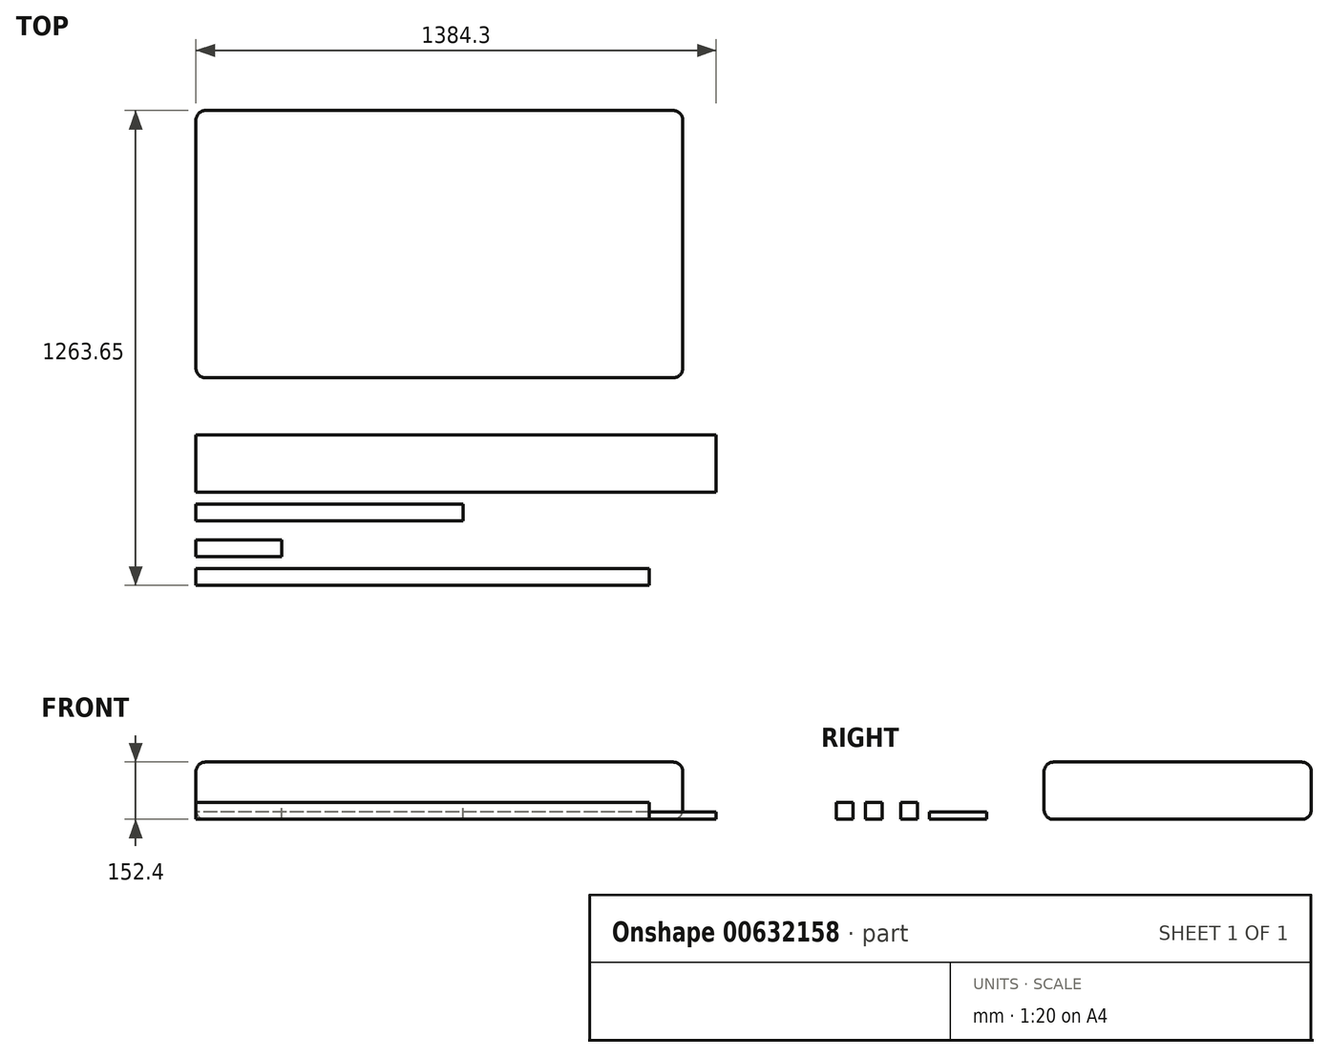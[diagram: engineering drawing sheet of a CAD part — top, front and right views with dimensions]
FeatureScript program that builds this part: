
annotation { "Feature Type Name" : "Feature", "Feature Type Description" : "" }
export const myFeature = defineFeature(function(context is Context, id is Id, definition is map)
    precondition{}
    {
        {
            var Q0;
            Q0=qCreatedBy(makeId("Right.planeOp"),FACE);
            var sketch = newSketch(context, id + "F0", { "sketchPlane" : qUnion([Q0])});
            skLineSegment(sketch, "E0.bottom", {"start": v(0, 0) * mm, "end": v(44.45, 0) * mm});
            skLineSegment(sketch, "E0.top", {"start": v(0, 44.45) * mm, "end": v(44.45, 44.45) * mm});
            skLineSegment(sketch, "E0.left", {"start": v(0, 0) * mm, "end": v(0, 44.45) * mm});
            skLineSegment(sketch, "E0.right", {"start": v(44.45, 0) * mm, "end": v(44.45, 44.45) * mm});
            skSolve(sketch);
        }
        {
            var Q0;
            Q0 = qSketchRegion(id + "F0", true);
            extrude(context, id + "F1", {"entities" : qUnion([Q0]), "depth" : 711.2 * mm, "offsetDistance" : 25.4 * mm});
        }
        {
            var Q0;
            Q0=makeQuery(id+"F1.opExtrude","SWEPT_BODY",BODY,{"disambiguationData":[OSD([sQuery(id+"F0.wireOp",EDGE,"E0.bottom"),sQuery(id+"F0.wireOp",EDGE,"E0.top"),sQuery(id+"F0.wireOp",EDGE,"E0.left"),sQuery(id+"F0.wireOp",EDGE,"E0.right")])]});
            transform(context, id + "F2", {"entities" : qUnion([Q0]), "transformType" : TransformType.TRANSLATION_3D, "dx" : 0 * mm, "dy" : 0 * mm, "dz" : 0 * mm, "makeCopy" : true});
        }
        {
            var Q0;
            Q0=qCreatedBy(makeId("Right.planeOp"),FACE);
            var sketch = newSketch(context, id + "F3", { "sketchPlane" : qUnion([Q0])});
            skLineSegment(sketch, "E1.bottom", {"start": v(-49.8, 0) * mm, "end": v(-94.25, 0) * mm});
            skLineSegment(sketch, "E1.top", {"start": v(-49.8, 44.45) * mm, "end": v(-94.25, 44.45) * mm});
            skLineSegment(sketch, "E1.left", {"start": v(-49.8, 0) * mm, "end": v(-49.8, 44.45) * mm});
            skLineSegment(sketch, "E1.right", {"start": v(-94.25, 0) * mm, "end": v(-94.25, 44.45) * mm});
            skSolve(sketch);
        }
        {
            var Q0;
            Q0 = qSketchRegion(id + "F3", true);
            extrude(context, id + "F4", {"entities" : qUnion([Q0]), "depth" : 228.6 * mm, "offsetDistance" : 25.4 * mm});
        }
        {
            var Q0;
            Q0=makeQuery(id+"F2.opPattern","COPY",BODY,{"derivedFrom":makeQuery(id+"F1.opExtrude","SWEPT_BODY",BODY,{"disambiguationData":[OSD([sQuery(id+"F0.wireOp",EDGE,"E0.bottom"),sQuery(id+"F0.wireOp",EDGE,"E0.top"),sQuery(id+"F0.wireOp",EDGE,"E0.left"),sQuery(id+"F0.wireOp",EDGE,"E0.right")])]}),"instanceName":"1"});
            deleteBodies(context, id + "F5", {"entities" : qUnion([Q0])});
        }
        {
            var Q0;
            Q0=qCreatedBy(makeId("Right.planeOp"),FACE);
            var sketch = newSketch(context, id + "F6", { "sketchPlane" : qUnion([Q0])});
            skLineSegment(sketch, "E2.bottom", {"start": v(76.2, 0) * mm, "end": v(228.6, 0) * mm});
            skLineSegment(sketch, "E2.top", {"start": v(76.2, 19.05) * mm, "end": v(228.6, 19.05) * mm});
            skLineSegment(sketch, "E2.left", {"start": v(76.2, 0) * mm, "end": v(76.2, 19.05) * mm});
            skLineSegment(sketch, "E2.right", {"start": v(228.6, 0) * mm, "end": v(228.6, 19.05) * mm});
            skSolve(sketch);
        }
        {
            var Q0;
            Q0 = qSketchRegion(id + "F6", true);
            extrude(context, id + "F7", {"entities" : qUnion([Q0]), "depth" : 1384.3 * mm, "offsetDistance" : 25.4 * mm});
        }
        {
            var Q0;
            Q0=qCreatedBy(makeId("Right.planeOp"),FACE);
            var sketch = newSketch(context, id + "F8", { "sketchPlane" : qUnion([Q0])});
            skLineSegment(sketch, "E3.bottom", {"start": v(-127, 0) * mm, "end": v(-171.45, 0) * mm});
            skLineSegment(sketch, "E3.top", {"start": v(-127, 44.45) * mm, "end": v(-171.45, 44.45) * mm});
            skLineSegment(sketch, "E3.left", {"start": v(-127, 0) * mm, "end": v(-127, 44.45) * mm});
            skLineSegment(sketch, "E3.right", {"start": v(-171.45, 0) * mm, "end": v(-171.45, 44.45) * mm});
            skSolve(sketch);
        }
        {
            var Q0;
            Q0=makeQuery(id+"F8.imprint","IMPRINT",FACE,{"disambiguationData":[TD([[makeQuery(id+"F8.imprint","IMPRINT",EDGE,{"derivedFrom":sQuery(id+"F8.wireOp",EDGE,"E3.bottom")}),-1.0]])]});
            extrude(context, id + "F9", {"entities" : qUnion([Q0]), "depth" : 1206.5 * mm, "offsetDistance" : 25.4 * mm});
        }
        {
            var Q0;
            Q0=qCreatedBy(makeId("Right.planeOp"),FACE);
            var sketch = newSketch(context, id + "F10", { "sketchPlane" : qUnion([Q0])});
            skLineSegment(sketch, "E4.bottom", {"start": v(381, 0) * mm, "end": v(1092.2, 0) * mm});
            skLineSegment(sketch, "E4.top", {"start": v(381, 152.4) * mm, "end": v(1092.2, 152.4) * mm});
            skLineSegment(sketch, "E4.left", {"start": v(381, 0) * mm, "end": v(381, 152.4) * mm});
            skLineSegment(sketch, "E4.right", {"start": v(1092.2, 0) * mm, "end": v(1092.2, 152.4) * mm});
            skSolve(sketch);
        }
        {
            var Q0;
            Q0 = qSketchRegion(id + "F10", true);
            extrude(context, id + "F11", {"entities" : qUnion([Q0]), "depth" : 1295.4 * mm, "offsetDistance" : 25.4 * mm});
        }
        {
            var Q0;
            Q0=makeQuery(id+"F11.opExtrude","SWEPT_EDGE",EDGE,{"disambiguationData":[OSD([sQuery(id+"F10.wireOp",EDGE,"E4.top"),sQuery(id+"F10.wireOp",EDGE,"E4.left")])]});
            var Q1;
            Q1=makeQuery(id+"F11.opExtrude","CAP_EDGE",EDGE,{"disambiguationData":[OSD([sQuery(id+"F10.wireOp",EDGE,"E4.top")])],"isStart":true});
            var Q2;
            Q2=makeQuery(id+"F11.opExtrude","SWEPT_EDGE",EDGE,{"disambiguationData":[OSD([sQuery(id+"F10.wireOp",EDGE,"E4.top"),sQuery(id+"F10.wireOp",EDGE,"E4.right")])]});
            var Q3;
            Q3=makeQuery(id+"F11.opExtrude","CAP_EDGE",EDGE,{"disambiguationData":[OSD([sQuery(id+"F10.wireOp",EDGE,"E4.top")])],"isStart":false});
            var Q4;
            Q4=makeQuery(id+"F11.opExtrude","CAP_EDGE",EDGE,{"disambiguationData":[OSD([sQuery(id+"F10.wireOp",EDGE,"E4.bottom")])],"isStart":false});
            var Q5;
            Q5=makeQuery(id+"F11.opExtrude","SWEPT_EDGE",EDGE,{"disambiguationData":[OSD([sQuery(id+"F10.wireOp",EDGE,"E4.bottom"),sQuery(id+"F10.wireOp",EDGE,"E4.left")])]});
            var Q6;
            Q6=makeQuery(id+"F11.opExtrude","SWEPT_EDGE",EDGE,{"disambiguationData":[OSD([sQuery(id+"F10.wireOp",EDGE,"E4.bottom"),sQuery(id+"F10.wireOp",EDGE,"E4.right")])]});
            var Q7;
            Q7=makeQuery(id+"F11.opExtrude","CAP_EDGE",EDGE,{"disambiguationData":[OSD([sQuery(id+"F10.wireOp",EDGE,"E4.bottom")])],"isStart":true});
            var Q8;
            Q8=makeQuery(id+"F11.opExtrude","CAP_EDGE",EDGE,{"disambiguationData":[OSD([sQuery(id+"F10.wireOp",EDGE,"E4.right")])],"isStart":true});
            var Q9;
            Q9=makeQuery(id+"F11.opExtrude","CAP_EDGE",EDGE,{"disambiguationData":[OSD([sQuery(id+"F10.wireOp",EDGE,"E4.right")])],"isStart":false});
            var Q10;
            Q10=makeQuery(id+"F11.opExtrude","CAP_EDGE",EDGE,{"disambiguationData":[OSD([sQuery(id+"F10.wireOp",EDGE,"E4.left")])],"isStart":true});
            var Q11;
            Q11=makeQuery(id+"F11.opExtrude","CAP_EDGE",EDGE,{"disambiguationData":[OSD([sQuery(id+"F10.wireOp",EDGE,"E4.left")])],"isStart":false});
            fillet(context, id + "F12", {"entities" : qUnion([Q0, Q1, Q2, Q3, Q4, Q5, Q6, Q7, Q8, Q9, Q10, Q11]), "radius" : 25.4 * mm, "tangentPropagation" : true, "allowEdgeOverflow" : false});
        }
    });
